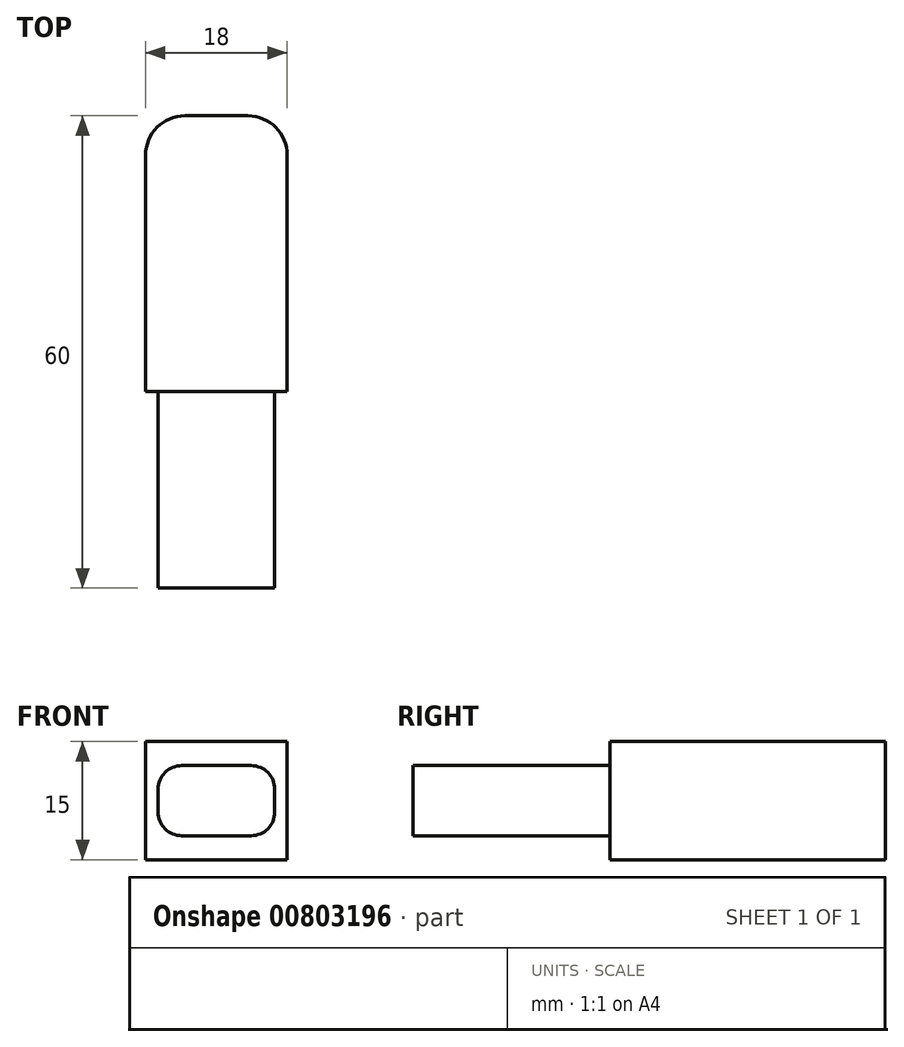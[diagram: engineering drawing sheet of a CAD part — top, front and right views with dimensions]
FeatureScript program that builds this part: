
annotation { "Feature Type Name" : "Feature", "Feature Type Description" : "" }
export const myFeature = defineFeature(function(context is Context, id is Id, definition is map)
    precondition{}
    {
        {
            var Q0;
            Q0=qCreatedBy(makeId("Top.planeOp"),FACE);
            var sketch = newSketch(context, id + "F0", { "sketchPlane" : qUnion([Q0])});
            skLineSegment(sketch, "E0.bottom", {"start": v(0, 0) * mm, "end": v(18, 0) * mm});
            skLineSegment(sketch, "E0.top", {"start": v(5, 35) * mm, "end": v(13, 35) * mm});
            skLineSegment(sketch, "E0.left", {"start": v(0, 0) * mm, "end": v(0, 30) * mm});
            skLineSegment(sketch, "E0.right", {"start": v(18, 0) * mm, "end": v(18, 30) * mm});
            skPoint(sketch, "E1.visualSharp", {"position": v(0, 35) * mm});
            skArc(sketch, "E1.filletArc", {"start": v(5, 35) * mm, "mid": v(1.46, 33.54) * mm, "end": v(0, 30) * mm});
            skPoint(sketch, "E2.visualSharp", {"position": v(18, 35) * mm});
            skArc(sketch, "E2.filletArc", {"start": v(18, 30) * mm, "mid": v(16.54, 33.54) * mm, "end": v(13, 35) * mm});
            skSolve(sketch);
        }
        {
            var Q0;
            Q0 = qSketchRegion(id + "F0", true);
            extrude(context, id + "F1", {"entities" : qUnion([Q0]), "depth" : 15 * mm, "offsetDistance" : 25 * mm});
        }
        {
            var Q0;
            Q0=makeQuery(id+"F1.opExtrude","SWEPT_FACE",FACE,{"disambiguationData":[OSD([sQuery(id+"F0.wireOp",EDGE,"E0.bottom")])]});
            var sketch = newSketch(context, id + "F2", { "sketchPlane" : qUnion([Q0])});
            skLineSegment(sketch, "E3", {"start": v(0, 0) * mm, "end": v(18, 15) * mm, "construction": true});
            skLineSegment(sketch, "E4.bottom", {"start": v(13.4, 11.95) * mm, "end": v(4.6, 11.95) * mm});
            skLineSegment(sketch, "E4.top", {"start": v(13.4, 3.05) * mm, "end": v(4.6, 3.05) * mm});
            skLineSegment(sketch, "E4.left", {"start": v(16.4, 8.95) * mm, "end": v(16.4, 6.05) * mm});
            skLineSegment(sketch, "E4.right", {"start": v(1.6, 8.95) * mm, "end": v(1.6, 6.05) * mm});
            skPoint(sketch, "E4.middle", {"position": v(9, 7.5) * mm});
            skPoint(sketch, "E5.visualSharp", {"position": v(1.6, 11.95) * mm});
            skArc(sketch, "E5.filletArc", {"start": v(4.6, 11.95) * mm, "mid": v(2.47, 11.07) * mm, "end": v(1.6, 8.95) * mm});
            skPoint(sketch, "E6.visualSharp", {"position": v(1.6, 3.05) * mm});
            skArc(sketch, "E6.filletArc", {"start": v(1.6, 6.05) * mm, "mid": v(2.47, 3.93) * mm, "end": v(4.6, 3.05) * mm});
            skPoint(sketch, "E7.visualSharp", {"position": v(16.4, 11.95) * mm});
            skArc(sketch, "E7.filletArc", {"start": v(16.4, 8.95) * mm, "mid": v(15.53, 11.07) * mm, "end": v(13.4, 11.95) * mm});
            skPoint(sketch, "E8.visualSharp", {"position": v(16.4, 3.05) * mm});
            skArc(sketch, "E8.filletArc", {"start": v(13.4, 3.05) * mm, "mid": v(15.53, 3.93) * mm, "end": v(16.4, 6.05) * mm});
            skSolve(sketch);
        }
        {
            var Q0;
            Q0 = qSketchRegion(id + "F2", true);
            extrude(context, id + "F3", {"entities" : qUnion([Q0]), "operationType" : NewBodyOperationType.ADD, "depth" : 25 * mm, "offsetDistance" : 25 * mm});
        }
    });
